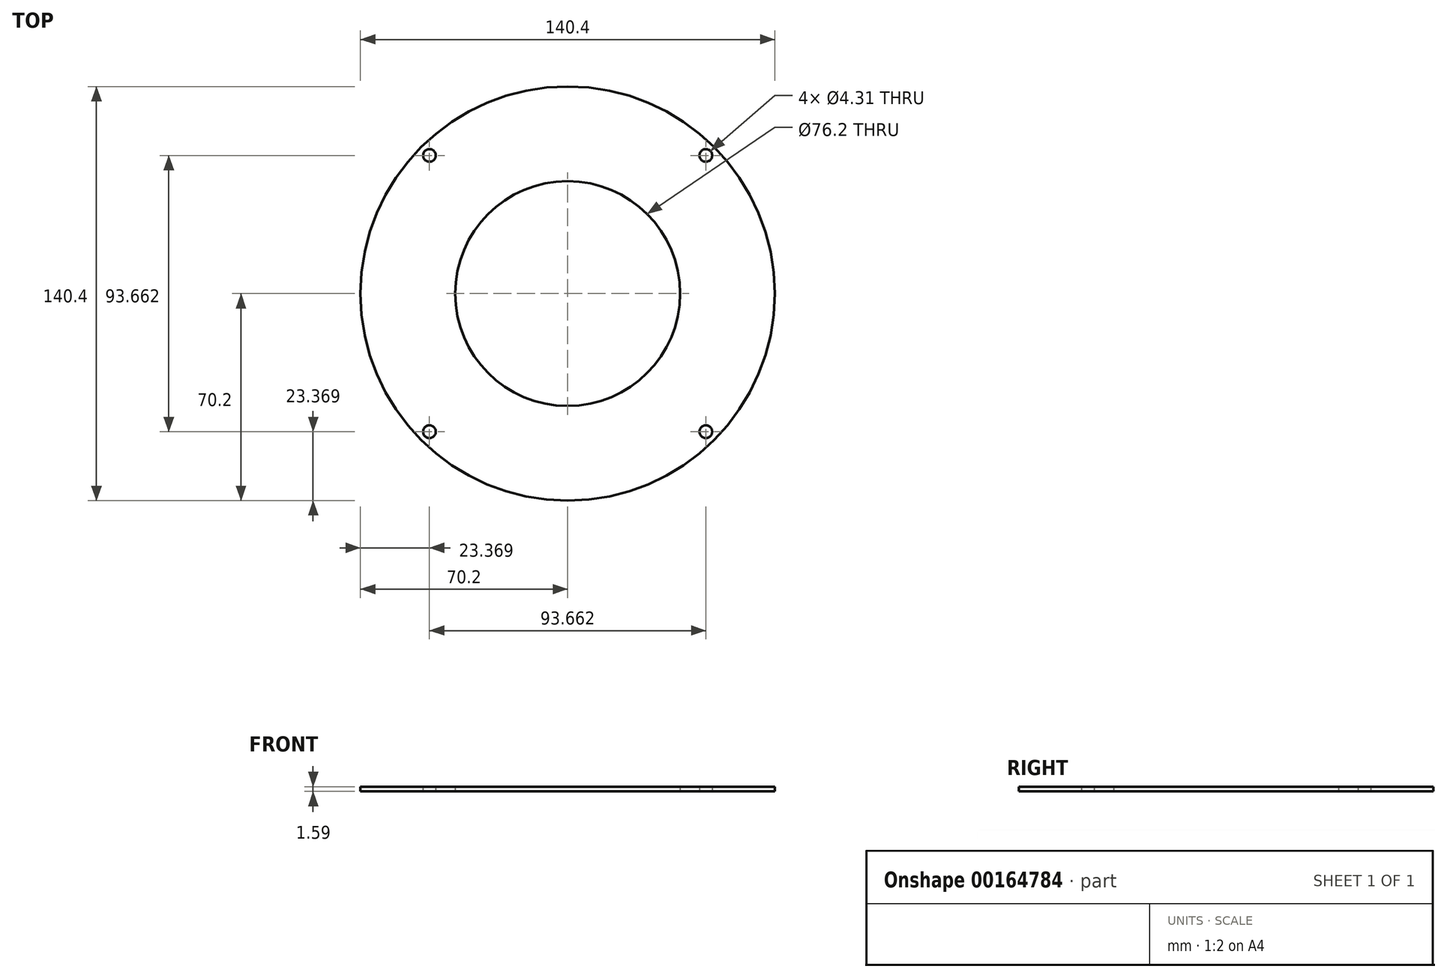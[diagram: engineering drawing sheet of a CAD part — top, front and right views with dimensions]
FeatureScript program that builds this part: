
annotation { "Feature Type Name" : "Feature", "Feature Type Description" : "" }
export const myFeature = defineFeature(function(context is Context, id is Id, definition is map)
    precondition{}
    {
        {
            var Q0;
            Q0=qCreatedBy(makeId("Top.planeOp"),FACE);
            var sketch = newSketch(context, id + "F0", { "sketchPlane" : qUnion([Q0])});
            skCircle(sketch, "E0", {"center": v(0, 0) * mm, "radius": 70.2 * mm});
            skLineSegment(sketch, "E1.bottom", {"start": v(46.83, 46.83) * mm, "end": v(46.83, -46.83) * mm, "construction": true});
            skLineSegment(sketch, "E1.top", {"start": v(-46.83, 46.83) * mm, "end": v(-46.83, -46.83) * mm, "construction": true});
            skLineSegment(sketch, "E1.left", {"start": v(46.83, 46.83) * mm, "end": v(-46.83, 46.83) * mm, "construction": true});
            skLineSegment(sketch, "E1.right", {"start": v(46.83, -46.83) * mm, "end": v(-46.83, -46.83) * mm, "construction": true});
            skCircle(sketch, "E2", {"center": v(-46.83, -46.83) * mm, "radius": 2.15 * mm});
            skCircle(sketch, "E3", {"center": v(-46.83, 46.83) * mm, "radius": 2.15 * mm});
            skCircle(sketch, "E4", {"center": v(46.83, 46.83) * mm, "radius": 2.15 * mm});
            skCircle(sketch, "E5", {"center": v(46.83, -46.83) * mm, "radius": 2.15 * mm});
            skCircle(sketch, "E6", {"center": v(-46.83, 46.83) * mm, "radius": 3.97 * mm, "construction": true});
            skCircle(sketch, "E7", {"center": v(0, 0) * mm, "radius": 38.1 * mm});
            skSolve(sketch);
        }
        {
            var Q0;
            Q0=makeQuery(id+"F0.imprint","IMPRINT",FACE,{"disambiguationData":[TD([[makeQuery(id+"F0.imprint","IMPRINT",EDGE,{"derivedFrom":sQuery(id+"F0.wireOp",EDGE,"E0")}),1.0]])]});
            extrude(context, id + "F1", {"entities" : qUnion([Q0]), "depth" : 1.59 * mm});
        }
    });
